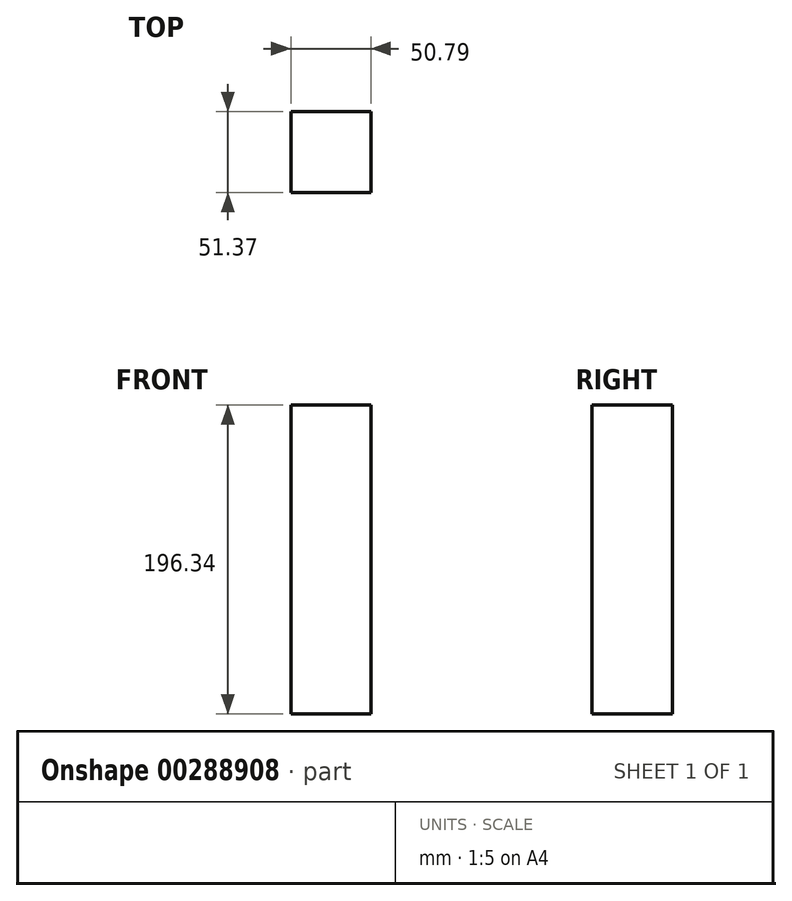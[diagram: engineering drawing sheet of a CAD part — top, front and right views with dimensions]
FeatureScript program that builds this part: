
annotation { "Feature Type Name" : "Feature", "Feature Type Description" : "" }
export const myFeature = defineFeature(function(context is Context, id is Id, definition is map)
    precondition{}
    {
        {
            var Q0;
            Q0=qCreatedBy(makeId("Top.planeOp"),FACE);
            var sketch = newSketch(context, id + "F0", { "sketchPlane" : qUnion([Q0])});
            skLineSegment(sketch, "E0.bottom", {"start": v(0, 0) * mm, "end": v(50.8, 0) * mm});
            skLineSegment(sketch, "E0.top", {"start": v(0, 51.37) * mm, "end": v(50.8, 51.37) * mm});
            skLineSegment(sketch, "E0.left", {"start": v(0, 0) * mm, "end": v(0, 51.37) * mm});
            skLineSegment(sketch, "E0.right", {"start": v(50.8, 0) * mm, "end": v(50.8, 51.37) * mm});
            skSolve(sketch);
        }
        {
            var Q0;
            Q0 = qSketchRegion(id + "F0", true);
            extrude(context, id + "F1", {"entities" : qUnion([Q0]), "depth" : 196.34 * mm});
        }
    });
